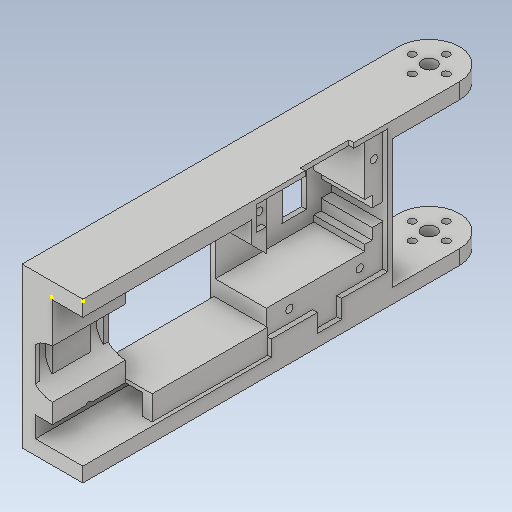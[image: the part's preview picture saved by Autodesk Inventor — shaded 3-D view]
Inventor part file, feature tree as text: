
AUTODESK INVENTOR PART (.ipt)
format: ipt  version: 2020.1 (Build 241239000, 239)  size: 579,072 bytes
history: native  units: mm
features: sketch x27, extrude x25, other x16, mirror x2, chamfer x1
ambient origin geometry x8: Origin, YZ Plane, XZ Plane, XY Plane, X Axis, Y Axis, Z Axis, Center Point
bodies: Body1 (feature_tree), Body2 (feature_tree)
feature tree (71):
  other  "Sólido1"
  extrude  "Extrusión1"  Depth=25.0mm
  sketch  "Boceto2"  dims[d2=6.0mm d7=3.0mm]
  extrude  "Extrusión2"  Depth=3.0mm
  extrude  "Extrusión3"  Depth=5.0mm TaperAngle=0.0deg
  sketch  "Boceto5"  dims[d13=12.5mm d14=0.0mm d15=5.0mm d16=0.0mm]
  extrude  "Extrusión4"  Depth=33.0mm
  extrude  "Extrusión6"  Depth=5.0mm TaperAngle=0.0deg
  extrude  "Extrusión7"  Depth=7.0mm
  mirror  "Simetría1"
  mirror  "Simetría2"
  extrude  "Extrusión8"  Depth=2.0mm TaperAngle=0.0deg
  other  "Edición directa1"
  other  "Edición directa2"
  other  "Edición directa3"
  other  "Edición directa4"
  extrude  "Extrusión9"  Depth=2.0mm TaperAngle=0.0deg
  extrude  "Extrusión10"  Depth=0.5mm TaperAngle=0.0deg
  other  "Edición directa5"
  extrude  "Extrusión11"  TaperAngle=0.0deg  [1 undecoded]
  extrude  "Extrusión14"  Depth=50.0mm
  extrude  "Extrusión15"  Depth=10.0mm
  extrude  "Extrusión16"  Depth=2.5mm
  extrude  "Extrusión17"  Depth=5.0mm
  chamfer  "Chaflán1"  Distance=23.0mm
  extrude  "Extrusión18"  Depth=10.0mm
  extrude  "Extrusión19"  Depth=2.0mm TaperAngle=0.0deg
  extrude  "Extrusión20"  Depth=10.0mm
  extrude  "Extrusión21"  Depth=10.0mm
  extrude  "Extrusión22"  Depth=24.0mm
  other  "Edición directa6"
  other  "Edición directa7"
  extrude  "Extrusión23"  Depth=5.0mm
  extrude  "Extrusión24"  Depth=2.0mm TaperAngle=0.0deg
  extrude  "Extrusión25"  Depth=9.5mm
  extrude  "Extrusión26"  Depth=9.5mm
  extrude  "Extrusión27"  Depth=10.0mm
  extrude  "Extrusión28"  Depth=3.75mm
  sketch  "Boceto1"  dims[d0=25.0mm d1=140.0mm]
  sketch  "Boceto3"  dims[d8=3.0mm d9=5.0mm d10=0.0mm]
  sketch  "Boceto4"  dims[d11=55.0mm d12=33.0mm]
  sketch  "Boceto6"  dims[d19=33.0mm d20=0.0mm d22=7.0mm]
  sketch  "Boceto7"  dims[d23=7.0mm d30=2.0mm d31=0.0mm]
  sketch  "Boceto10"  dims[d32=2.0mm d33=0.0mm d34=2.0mm d35=0.0mm]
  sketch  "Boceto11"  dims[d36=0.0mm d37=0.0mm d38=7.0mm d39=0.0mm d40=0.0mm d41=0.5mm]
  sketch  "Boceto12"  dims[d42=0.0mm d43=0.0mm d44=9.5mm d45=0.0mm d46=0.0mm d47=-3.0mm]
  sketch  "Boceto13"  dims[d48=25.0mm d49=50.0mm]
  sketch  "Boceto15"  dims[d50=25.0mm d51=0.0mm d52=10.0mm]
  sketch  "Boceto18"  dims[d58=40.5mm d59=2.5mm]
  sketch  "Boceto19"  dims[d61=3.0mm d62=5.0mm]
  sketch  "Boceto20"  dims[d63=5.0mm]
  sketch  "Boceto21"  dims[d64=5.0mm]
  sketch  "Boceto22"  dims[d65=41.0mm d66=23.0mm d67=0.0mm]
  sketch  "Boceto23"  dims[d68=0.0mm d69=0.0mm d70=0.5mm d71=10.0mm]
  sketch  "Boceto24"  dims[d72=5.0mm d74=2.0mm d75=0.0mm]
  sketch  "Boceto25"  dims[d82=5.0mm d83=10.0mm]
  sketch  "Boceto26"  dims[d84=6.0mm d85=10.0mm]
  sketch  "Boceto27"  dims[d86=2.0mm d87=0.0mm d88=24.0mm]
  sketch  "Boceto28"  dims[d89=5.0mm d90=5.0mm]
  sketch  "Boceto29"  dims[d91=10.0mm d92=2.0mm d93=0.0mm]
  sketch  "Boceto30"  dims[d94=5.0mm d95=9.5mm]
  sketch  "Boceto31"  dims[d96=3.0mm d97=9.5mm]
  sketch  "Boceto32"  dims[d98=3.0mm d99=10.0mm d100=3.75mm d101=3.0mm d102=23.0mm d103=0.0mm d104=16.0mm d105=8.0mm d106=25.0mm d107=0.0mm d108=6.0mm d109=2.0mm d110=45.0deg d111=4.0mm d112=10.0mm d113=2.0mm d114=0.0mm d115=5.0mm d116=3.0mm d117=3.0mm d118=23.0mm d119=0.0mm d120=3.5mm d121=3.5mm d122=3.5mm d123=3.5mm d124=2.0mm d125=0.0mm d126=3.0mm d127=3.0mm d128=12.5mm d129=0.0mm d130=3.5mm d131=3.5mm d132=2.0mm d133=0.0mm d134=0.0mm d135=0.0mm d136=1.0mm d137=0.0mm d138=0.0mm d139=1.0mm d140=0.0mm d141=-15.0mm d142=0.0mm d145=8.5mm d146=30.0mm d147=0.0mm d148=1.5mm d149=22.0mm d150=10.0mm d151=47.5mm d152=0.0mm d153=7.0mm d154=97.5mm d155=0.0mm d156=1.5mm d157=7.0mm d158=5.0mm d159=19.0mm d161=13.5mm d162=4.0mm d163=0.0mm d164=4.0mm d165=8.0mm d166=18.0mm d167=10.0mm d168=2.0mm d169=0.0mm d170=2.5mm d171=3.0mm d172=4.5mm d173=1.0mm d174=4.5mm d175=21.0mm d176=0.0mm]
  other  "Desplazar1"
  other  "Desplazar2"
  other  "Desplazar3"
  other  "Desplazar4"
  other  "Desplazar5"
  other  "Desplazar6"
  other  "Desplazar7"
  other  "Desplazar8"
note: 1 required parameter value undecoded (feature->parameter linkage not recoverable at this tier; creation-order binding heuristic only, values carry confidence <= 0.55)
